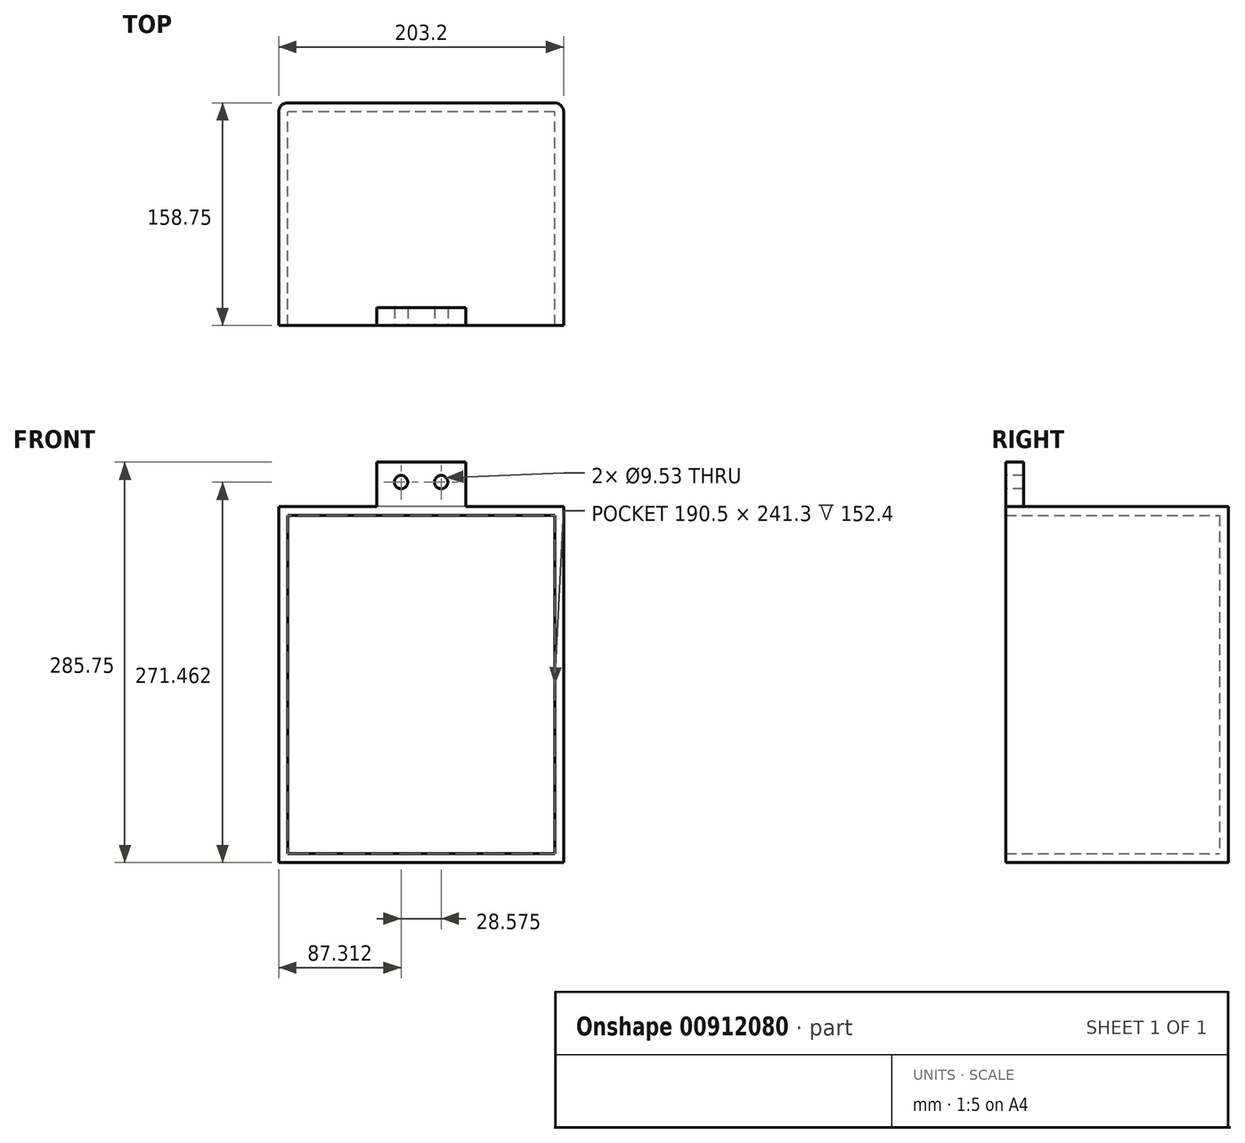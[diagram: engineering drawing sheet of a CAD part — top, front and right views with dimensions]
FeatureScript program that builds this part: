
annotation { "Feature Type Name" : "Feature", "Feature Type Description" : "" }
export const myFeature = defineFeature(function(context is Context, id is Id, definition is map)
    precondition{}
    {
        {
            var Q0;
            Q0=qCreatedBy(makeId("Front.planeOp"),FACE);
            var sketch = newSketch(context, id + "F0", { "sketchPlane" : qUnion([Q0])});
            skLineSegment(sketch, "E0.bottom", {"start": v(101.6, 127) * mm, "end": v(-101.6, 127) * mm});
            skLineSegment(sketch, "E0.top", {"start": v(101.6, -127) * mm, "end": v(-101.6, -127) * mm});
            skLineSegment(sketch, "E0.left", {"start": v(101.6, 127) * mm, "end": v(101.6, -127) * mm});
            skLineSegment(sketch, "E0.right", {"start": v(-101.6, 127) * mm, "end": v(-101.6, -127) * mm});
            skPoint(sketch, "E0.middle", {"position": v(0, 0) * mm});
            skLineSegment(sketch, "E1.bottom", {"start": v(95.25, 120.65) * mm, "end": v(-95.25, 120.65) * mm});
            skLineSegment(sketch, "E1.top", {"start": v(95.25, -120.65) * mm, "end": v(-95.25, -120.65) * mm});
            skLineSegment(sketch, "E1.left", {"start": v(95.25, 120.65) * mm, "end": v(95.25, -120.65) * mm});
            skLineSegment(sketch, "E1.right", {"start": v(-95.25, 120.65) * mm, "end": v(-95.25, -120.65) * mm});
            skSolve(sketch);
        }
        {
            var Q0;
            Q0 = qSketchRegion(id + "F0", true);
            extrude(context, id + "F1", {"entities" : qUnion([Q0]), "depth" : 152.4 * mm, "offsetDistance" : 25.4 * mm});
        }
        {
            var Q0;
            Q0=makeQuery(id+"F1.opExtrude","CAP_FACE",FACE,{"disambiguationData":[OSD([sQuery(id+"F0.wireOp",EDGE,"E0.bottom"),sQuery(id+"F0.wireOp",EDGE,"E0.top"),sQuery(id+"F0.wireOp",EDGE,"E0.left"),sQuery(id+"F0.wireOp",EDGE,"E0.right"),sQuery(id+"F0.wireOp",EDGE,"E1.bottom"),sQuery(id+"F0.wireOp",EDGE,"E1.top"),sQuery(id+"F0.wireOp",EDGE,"E1.left"),sQuery(id+"F0.wireOp",EDGE,"E1.right")])],"isStart":true});
            var sketch = newSketch(context, id + "F2", { "sketchPlane" : qUnion([Q0])});
            skLineSegment(sketch, "E2.bottom", {"start": v(-101.6, 127) * mm, "end": v(101.6, 127) * mm});
            skLineSegment(sketch, "E2.top", {"start": v(-101.6, -127) * mm, "end": v(101.6, -127) * mm});
            skLineSegment(sketch, "E2.left", {"start": v(-101.6, 127) * mm, "end": v(-101.6, -127) * mm});
            skLineSegment(sketch, "E2.right", {"start": v(101.6, 127) * mm, "end": v(101.6, -127) * mm});
            skSolve(sketch);
        }
        {
            var Q0;
            Q0 = qSketchRegion(id + "F2", true);
            extrude(context, id + "F3", {"entities" : qUnion([Q0]), "operationType" : NewBodyOperationType.ADD, "depth" : 6.35 * mm, "offsetDistance" : 25.4 * mm});
        }
        {
            var Q0;
            Q0=makeQuery(id+"F1.opExtrude","CAP_EDGE",EDGE,{"disambiguationData":[OSD([sQuery(id+"F0.wireOp",EDGE,"E1.right")])],"isStart":true});
            var Q1;
            Q1=makeQuery(id+"F1.opExtrude","CAP_EDGE",EDGE,{"disambiguationData":[OSD([sQuery(id+"F0.wireOp",EDGE,"E1.left")])],"isStart":true});
            var Q2;
            Q2=makeQuery(id+"F3.opExtrude","CAP_EDGE",EDGE,{"disambiguationData":[OSD([sQuery(id+"F2.wireOp",EDGE,"E2.right")])],"isStart":false});
            var Q3;
            Q3=makeQuery(id+"F3.opExtrude","CAP_EDGE",EDGE,{"disambiguationData":[OSD([sQuery(id+"F2.wireOp",EDGE,"E2.left")])],"isStart":false});
            fillet(context, id + "F4", {"entities" : qUnion([Q0, Q1, Q2, Q3]), "radius" : 6.35 * mm, "tangentPropagation" : true, "allowEdgeOverflow" : false});
        }
        {
            var Q0;
            Q0=makeQuery(id+"F1.opExtrude","CAP_FACE",FACE,{"disambiguationData":[OSD([sQuery(id+"F0.wireOp",EDGE,"E0.bottom"),sQuery(id+"F0.wireOp",EDGE,"E0.top"),sQuery(id+"F0.wireOp",EDGE,"E0.left"),sQuery(id+"F0.wireOp",EDGE,"E0.right"),sQuery(id+"F0.wireOp",EDGE,"E1.bottom"),sQuery(id+"F0.wireOp",EDGE,"E1.top"),sQuery(id+"F0.wireOp",EDGE,"E1.left"),sQuery(id+"F0.wireOp",EDGE,"E1.right")])],"isStart":false});
            var sketch = newSketch(context, id + "F5", { "sketchPlane" : qUnion([Q0])});
            skLineSegment(sketch, "E3.bottom", {"start": v(-31.75, 120.65) * mm, "end": v(31.75, 120.65) * mm});
            skLineSegment(sketch, "E3.top", {"start": v(-31.75, 158.75) * mm, "end": v(31.75, 158.75) * mm});
            skLineSegment(sketch, "E3.left", {"start": v(-31.75, 120.65) * mm, "end": v(-31.75, 158.75) * mm});
            skLineSegment(sketch, "E3.right", {"start": v(31.75, 120.65) * mm, "end": v(31.75, 158.75) * mm});
            skLineSegment(sketch, "E4", {"start": v(31.75, 144.46) * mm, "end": v(-31.75, 144.46) * mm, "construction": true});
            skCircle(sketch, "E5", {"center": v(-14.29, 144.46) * mm, "radius": 4.76 * mm});
            skCircle(sketch, "E6", {"center": v(14.29, 144.46) * mm, "radius": 4.76 * mm});
            skSolve(sketch);
        }
        {
            var Q0;
            Q0 = qSketchRegion(id + "F5", true);
            extrude(context, id + "F6", {"entities" : qUnion([Q0]), "operationType" : NewBodyOperationType.ADD, "oppositeDirection" : true, "depth" : 12.7 * mm, "offsetDistance" : 25.4 * mm});
        }
    });
